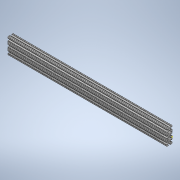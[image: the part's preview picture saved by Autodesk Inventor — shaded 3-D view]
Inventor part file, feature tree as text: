
AUTODESK INVENTOR PART (.ipt)
format: ipt  version: 2020 (Build 240168000, 168)  size: 384,000 bytes
history: native  units: in
note: dims shown in document units (in); Inventor stores cm internally (conversion verified against a paired STEP export)
features: sketch x2, extrude x1
ambient origin geometry x8: Origin, YZ Plane, XZ Plane, XY Plane, X Axis, Y Axis, Z Axis, Center Point
bodies: Solid1 (feature_tree)
feature tree (3):
  extrude  "Extrusion1"  [1 undecoded]
  sketch  "Sketch2"
  sketch  "Sketch1"  dims[d0=29.0in d1=0.0in]
note: 1 required parameter value undecoded (feature->parameter linkage not recoverable at this tier; creation-order binding heuristic only, values carry confidence <= 0.55)
